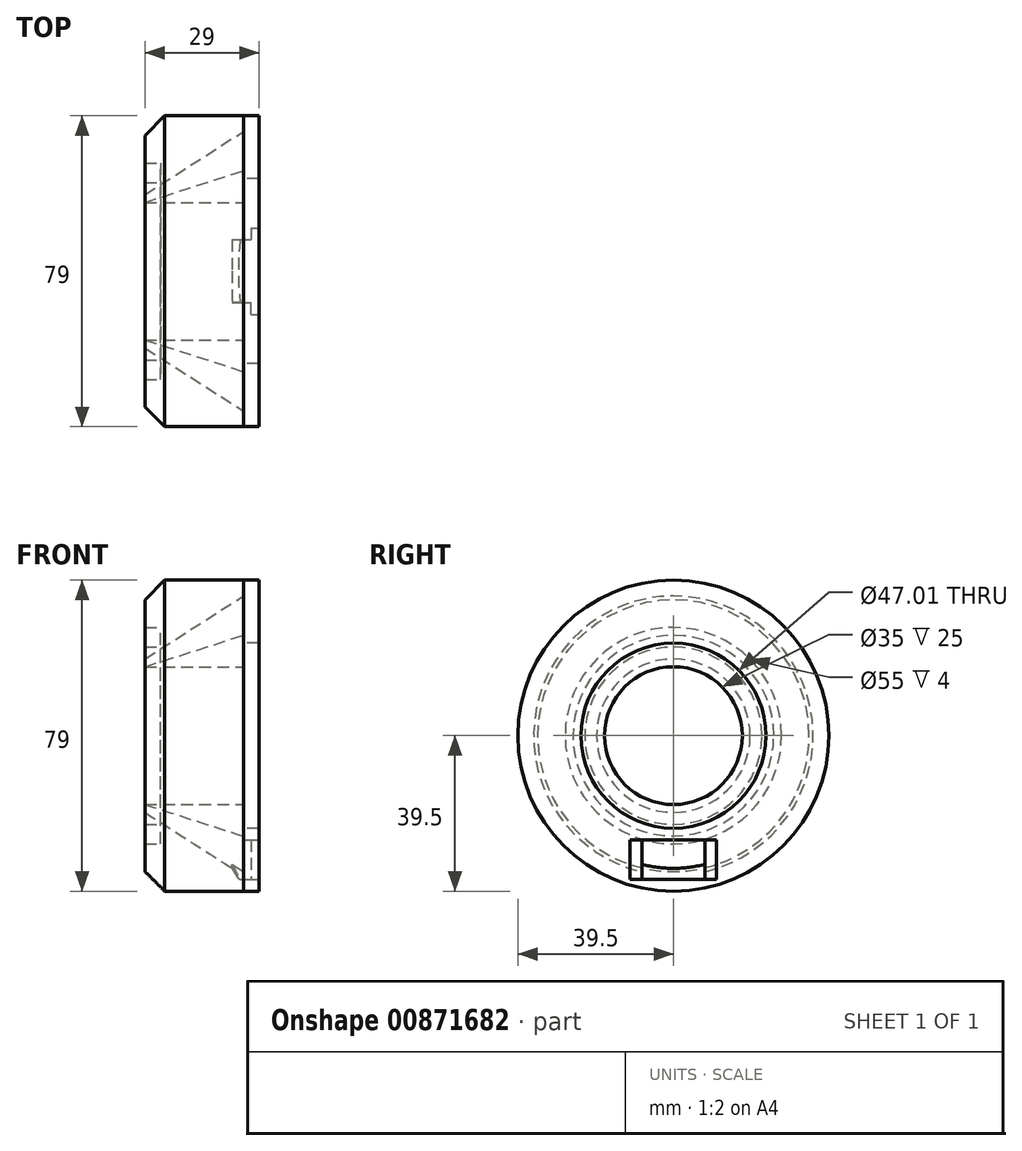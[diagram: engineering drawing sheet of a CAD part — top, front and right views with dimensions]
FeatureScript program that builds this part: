
annotation { "Feature Type Name" : "Feature", "Feature Type Description" : "" }
export const myFeature = defineFeature(function(context is Context, id is Id, definition is map)
    precondition{}
    {
        {
            var Q0;
            Q0=qCreatedBy(makeId("Top.planeOp"),FACE);
            var sketch = newSketch(context, id + "F0", { "sketchPlane" : qUnion([Q0])});
            skLineSegment(sketch, "E0.bottom", {"start": v(-12.5, 17.5) * mm, "end": v(12.5, 17.5) * mm});
            skLineSegment(sketch, "E0.top", {"start": v(-12.5, -17.5) * mm, "end": v(12.5, -17.5) * mm});
            skLineSegment(sketch, "E0.left", {"start": v(-12.5, 17.5) * mm, "end": v(-12.5, -17.5) * mm});
            skLineSegment(sketch, "E0.right", {"start": v(12.5, 17.5) * mm, "end": v(12.5, -17.5) * mm});
            skPoint(sketch, "E0.middle", {"position": v(0, 0) * mm});
            skLineSegment(sketch, "E1", {"start": v(12.5, 25.5) * mm, "end": v(12.5, 17.5) * mm});
            skLineSegment(sketch, "E2", {"start": v(12.5, 25.5) * mm, "end": v(-12.5, 17.5) * mm});
            skLineSegment(sketch, "E3", {"start": v(-12.5, 39.5) * mm, "end": v(12.5, 39.5) * mm});
            skLineSegment(sketch, "E4", {"start": v(12.5, 0) * mm, "end": v(-12.5, 0) * mm});
            skLineSegment(sketch, "E5.bottom", {"start": v(12.5, 17.5) * mm, "end": v(-12.5, 17.5) * mm});
            skLineSegment(sketch, "E5.top", {"start": v(12.5, 15.5) * mm, "end": v(-12.5, 15.5) * mm});
            skLineSegment(sketch, "E5.left", {"start": v(12.5, 17.5) * mm, "end": v(12.5, 15.5) * mm});
            skLineSegment(sketch, "E5.right", {"start": v(-12.5, 17.5) * mm, "end": v(-12.5, 15.5) * mm});
            skLineSegment(sketch, "E6", {"start": v(-12.5, 27.5) * mm, "end": v(-8.5, 27.5) * mm, "construction": true});
            skLineSegment(sketch, "E7", {"start": v(-8.5, 27.5) * mm, "end": v(-8.5, 22.5) * mm, "construction": true});
            skLineSegment(sketch, "E8", {"start": v(-8.5, 22.5) * mm, "end": v(-12.5, 22.5) * mm, "construction": true});
            skLineSegment(sketch, "E9", {"start": v(-12.5, 27.5) * mm, "end": v(-8.5, 27.5) * mm});
            skLineSegment(sketch, "E10", {"start": v(-8.5, 22.5) * mm, "end": v(-12.5, 22.5) * mm});
            skLineSegment(sketch, "E11", {"start": v(-8.5, 27.5) * mm, "end": v(-8.5, 22.5) * mm});
            skLineSegment(sketch, "E12", {"start": v(-12.5, 19.5) * mm, "end": v(-12.5, 22.5) * mm});
            skLineSegment(sketch, "E13", {"start": v(-12.5, 27.5) * mm, "end": v(-12.5, 39.5) * mm});
            skLineSegment(sketch, "E14", {"start": v(-12.5, 19.5) * mm, "end": v(12.5, 35.49) * mm});
            skLineSegment(sketch, "E15", {"start": v(12.5, 39.5) * mm, "end": v(12.5, 35.49) * mm});
            skLineSegment(sketch, "E16", {"start": v(-12.5, 22.5) * mm, "end": v(-12.5, -17.5) * mm});
            skLineSegment(sketch, "E17", {"start": v(-12.5, 39.5) * mm, "end": v(-12.5, 27.5) * mm, "construction": true});
            skLineSegment(sketch, "E18", {"start": v(-12.5, 27.5) * mm, "end": v(-12.5, 22.5) * mm, "construction": true});
            skLineSegment(sketch, "E19", {"start": v(-12.5, 27.5) * mm, "end": v(-12.5, 15.5) * mm, "construction": true});
            skSolve(sketch);
        }
        {
            var Q0;
            Q0=makeQuery(id+"F0.imprint","IMPRINT",FACE,{"disambiguationData":[TD([[makeQuery(id+"F0.imprint","IMPRINT",EDGE,{"derivedFrom":sQuery(id+"F0.wireOp",EDGE,"E5.bottom")}),1.0]])]});
            var Q1;
            Q1=makeQuery(id+"F0.imprint","IMPRINT",FACE,{"disambiguationData":[TD([[makeQuery(id+"F0.imprint","IMPRINT",EDGE,{"derivedFrom":sQuery(id+"F0.wireOp",EDGE,"E1")}),-1.0]])]});
            var Q2;
            Q2=makeQuery(id+"F0.imprint","IMPRINT",FACE,{"disambiguationData":[TD([[makeQuery(id+"F0.imprint","IMPRINT",EDGE,{"derivedFrom":sQuery(id+"F0.wireOp",EDGE,"E3")}),-1.0]])]});
            var Q3;
            Q3=sQuery(id+"F0.wireOp",EDGE,"E4");
            revolve(context, id + "F1", {"surfaceOperationType" : NewSurfaceOperationType.NEW, "entities" : qUnion([Q0, Q1, Q2]), "axis" : qUnion([Q3]), "revolveType" : RevolveType.FULL});
        }
        {
            var Q0;
            Q0=makeQuery(id+"F1.opRevolve","SWEPT_EDGE",EDGE,{"disambiguationData":[OSD([sQuery(id+"F0.wireOp",EDGE,"E3"),sQuery(id+"F0.wireOp",EDGE,"E13")])]});
            chamfer(context, id + "F2", {"entities" : qUnion([Q0]), "width" : 5 * mm, "tangentPropagation" : true});
        }
        {
            var Q0;
            Q0=makeQuery(id+"F1.opRevolve","SWEPT_FACE",FACE,{"disambiguationData":[OSD([sQuery(id+"F0.wireOp",EDGE,"E1"),sQuery(id+"F0.wireOp",EDGE,"E5.left")])]});
            var sketch = newSketch(context, id + "F3", { "sketchPlane" : qUnion([Q0])});
            skCircle(sketch, "E20", {"center": v(0, 0) * mm, "radius": 39.5 * mm});
            skLineSegment(sketch, "E21", {"start": v(-2.02, -25.42) * mm, "end": v(-2.02, -23.42) * mm, "construction": true});
            skCircle(sketch, "E22", {"center": v(0, 0) * mm, "radius": 23.5 * mm});
            skSolve(sketch);
        }
        {
            var Q0;
            Q0 = qSketchRegion(id + "F3", true);
            extrude(context, id + "F4", {"entities" : qUnion([Q0]), "depth" : 4 * mm, "offsetDistance" : 25 * mm});
        }
        {
            var Q0;
            Q0=makeQuery(id+"F4.opExtrude","CAP_FACE",FACE,{"disambiguationData":[OSD([sQuery(id+"F3.wireOp",EDGE,"E20"),sQuery(id+"F3.wireOp",EDGE,"E22")])],"isStart":false});
            var sketch = newSketch(context, id + "F5", { "sketchPlane" : qUnion([Q0])});
            skLineSegment(sketch, "E23", {"start": v(0, -23.5) * mm, "end": v(0, -39.5) * mm});
            skLineSegment(sketch, "E24.bottom", {"start": v(-8, -26.5) * mm, "end": v(8, -26.5) * mm});
            skLineSegment(sketch, "E24.top", {"start": v(-8, -36.5) * mm, "end": v(8, -36.5) * mm});
            skLineSegment(sketch, "E24.left", {"start": v(-8, -26.5) * mm, "end": v(-8, -36.5) * mm});
            skLineSegment(sketch, "E24.right", {"start": v(8, -26.5) * mm, "end": v(8, -36.5) * mm});
            skPoint(sketch, "E24.middle", {"position": v(0, -31.5) * mm});
            skLineSegment(sketch, "E25", {"start": v(-8, -26.5) * mm, "end": v(-11, -26.5) * mm});
            skLineSegment(sketch, "E26", {"start": v(-11, -26.5) * mm, "end": v(-11, -36.5) * mm});
            skLineSegment(sketch, "E27", {"start": v(-11, -36.5) * mm, "end": v(-8, -36.5) * mm});
            skLineSegment(sketch, "E28.MirrorCS", {"start": v(11, -26.5) * mm, "end": v(11, -36.5) * mm});
            skLineSegment(sketch, "E29.MirrorCS", {"start": v(8, -26.5) * mm, "end": v(11, -26.5) * mm});
            skLineSegment(sketch, "E30.MirrorCS", {"start": v(11, -36.5) * mm, "end": v(8, -36.5) * mm});
            skSolve(sketch);
        }
        {
            var Q0;
            {var subQ5=sQuery(id+"F5.wireOp",EDGE,"E24.left");Q0=makeQuery(id+"F5.imprint","IMPRINT",FACE,{"disambiguationData":[TD([[makeQuery(id+"F5.imprint","IMPRINT",EDGE,{"derivedFrom":subQ5}),1.0]])]});}
            var Q1;
            {var subQ5=sQuery(id+"F5.wireOp",EDGE,"E24.right");Q1=makeQuery(id+"F5.imprint","IMPRINT",FACE,{"disambiguationData":[TD([[makeQuery(id+"F5.imprint","IMPRINT",EDGE,{"derivedFrom":subQ5}),-1.0]])]});}
            extrude(context, id + "F6", {"entities" : qUnion([Q0, Q1]), "operationType" : NewBodyOperationType.REMOVE, "oppositeDirection" : true, "depth" : 4.5 * mm, "offsetDistance" : 25 * mm});
        }
        {
            var Q0;
            Q0=makeQuery(id+"F5.imprint","IMPRINT",FACE,{"disambiguationData":[TD([[makeQuery(id+"F5.imprint","IMPRINT",EDGE,{"derivedFrom":sQuery(id+"F5.wireOp",EDGE,"E24.left")}),-1.0]])]});
            var Q1;
            Q1=makeQuery(id+"F5.imprint","IMPRINT",FACE,{"disambiguationData":[TD([[makeQuery(id+"F5.imprint","IMPRINT",EDGE,{"derivedFrom":sQuery(id+"F5.wireOp",EDGE,"E24.right")}),1.0]])]});
            extrude(context, id + "F7", {"entities" : qUnion([Q0, Q1]), "operationType" : NewBodyOperationType.REMOVE, "oppositeDirection" : true, "depth" : 2 * mm, "offsetDistance" : 25 * mm});
        }
        {
            var Q0;
            Q0=makeQuery(id+"F6.boolean.opBoolean","INTERSECT",EDGE,{"derivedFrom":[makeQuery(id+"F1.opRevolve","SWEPT_FACE",FACE,{"disambiguationData":[OSD([sQuery(id+"F0.wireOp",EDGE,"E14")])]}),makeQuery(id+"F6.opExtrude","CAP_FACE",FACE,{"disambiguationData":[OSD([sQuery(id+"F5.wireOp",EDGE,"E24.bottom"),sQuery(id+"F5.wireOp",EDGE,"E24.top"),sQuery(id+"F5.wireOp",EDGE,"E24.left"),sQuery(id+"F5.wireOp",EDGE,"E24.right")])],"isStart":false})]});
            chamfer(context, id + "F8", {"entities" : qUnion([Q0]), "width" : 5 * mm, "tangentPropagation" : true});
        }
    });
